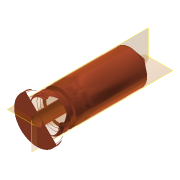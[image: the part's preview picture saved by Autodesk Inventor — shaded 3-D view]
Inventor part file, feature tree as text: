
AUTODESK INVENTOR PART (.ipt)
format: ipt  version: 2016 (Build 200138000, 138)  size: 175,616 bytes
history: native  units: mm
features: sketch x6, extrude x3, revolve x3, reference x2, chamfer x1
ambient origin geometry x8: Origin, YZ Plane, XZ Plane, XY Plane, X Axis, Y Axis, Z Axis, Center Point
bodies: Solid1 (feature_tree)
feature tree (15):
  extrude  "Extrusion1"  Depth=1.0mm TaperAngle=0.0deg
  extrude  "Extrusion2"  Depth=15.5mm TaperAngle=0.0deg
  extrude  "Extrusion3"  Depth=2.0mm TaperAngle=0.0deg
  revolve  "Revolution1"  [1 undecoded]
  revolve  "Revolution2"  Angle=90.0deg
  chamfer  "Chamfer1"  Angle=90.0deg  [1 undecoded]
  revolve  "Revolution3"  Angle=45.0deg
  sketch  "Sketch1"  dims[d0=8.0mm d1=1.0mm d2=0.0mm]
  sketch  "Sketch2"  dims[d3=6.0mm d4=15.5mm d5=0.0mm]
  sketch  "Sketch3"  dims[d6=2.0mm d7=21.0mm d8=0.0mm]
  sketch  "Sketch4"  dims[d9=6.981317mm d10=0.2mm]
  sketch  "Sketch5"  dims[d11=30.0deg d13=90.0deg]
  sketch  "Sketch6"  dims[d14=0.7mm d15=90.0deg d16=0.3mm d17=2.0mm d18=45.0deg d19=45.0deg d20=0.05mm d21=1.0mm d22=0.6mm d23=90.0deg]
  reference  "Reference1"
  reference  "Reference2"
note: 2 required parameter values undecoded (feature->parameter linkage not recoverable at this tier; creation-order binding heuristic only, values carry confidence <= 0.55)